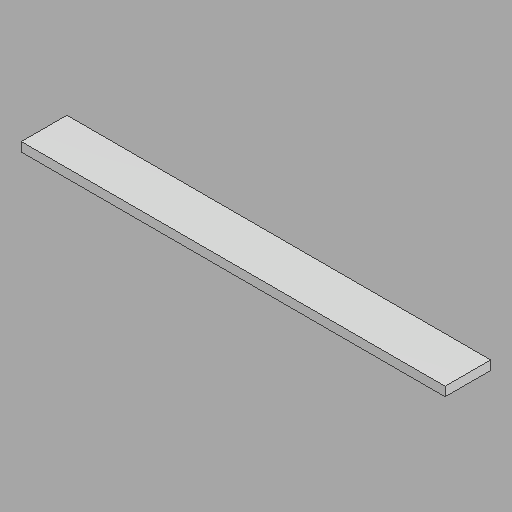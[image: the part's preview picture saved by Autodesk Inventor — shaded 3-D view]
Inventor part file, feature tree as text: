
AUTODESK INVENTOR PART (.ipt)
format: ipt  version: 2022.2 (Build 262287010, 287A)  size: 112,128 bytes
history: native  units: in
note: dims shown in document units (in); Inventor stores cm internally (conversion verified against a paired STEP export)
features: direct_edit x1, other x1, revolve x1
ambient origin geometry x8: Origin, YZ Plane, XZ Plane, XY Plane, X Axis, Y Axis, Z Axis, Center Point
bodies: Solid1 (feature_tree)
feature tree (3):
  direct_edit  "Direct Edit1"
  other  "R Vert rect jamb lower"
  revolve  "Rotate1"  [1 undecoded]
note: 1 required parameter value undecoded (feature->parameter linkage not recoverable at this tier; creation-order binding heuristic only, values carry confidence <= 0.55)
